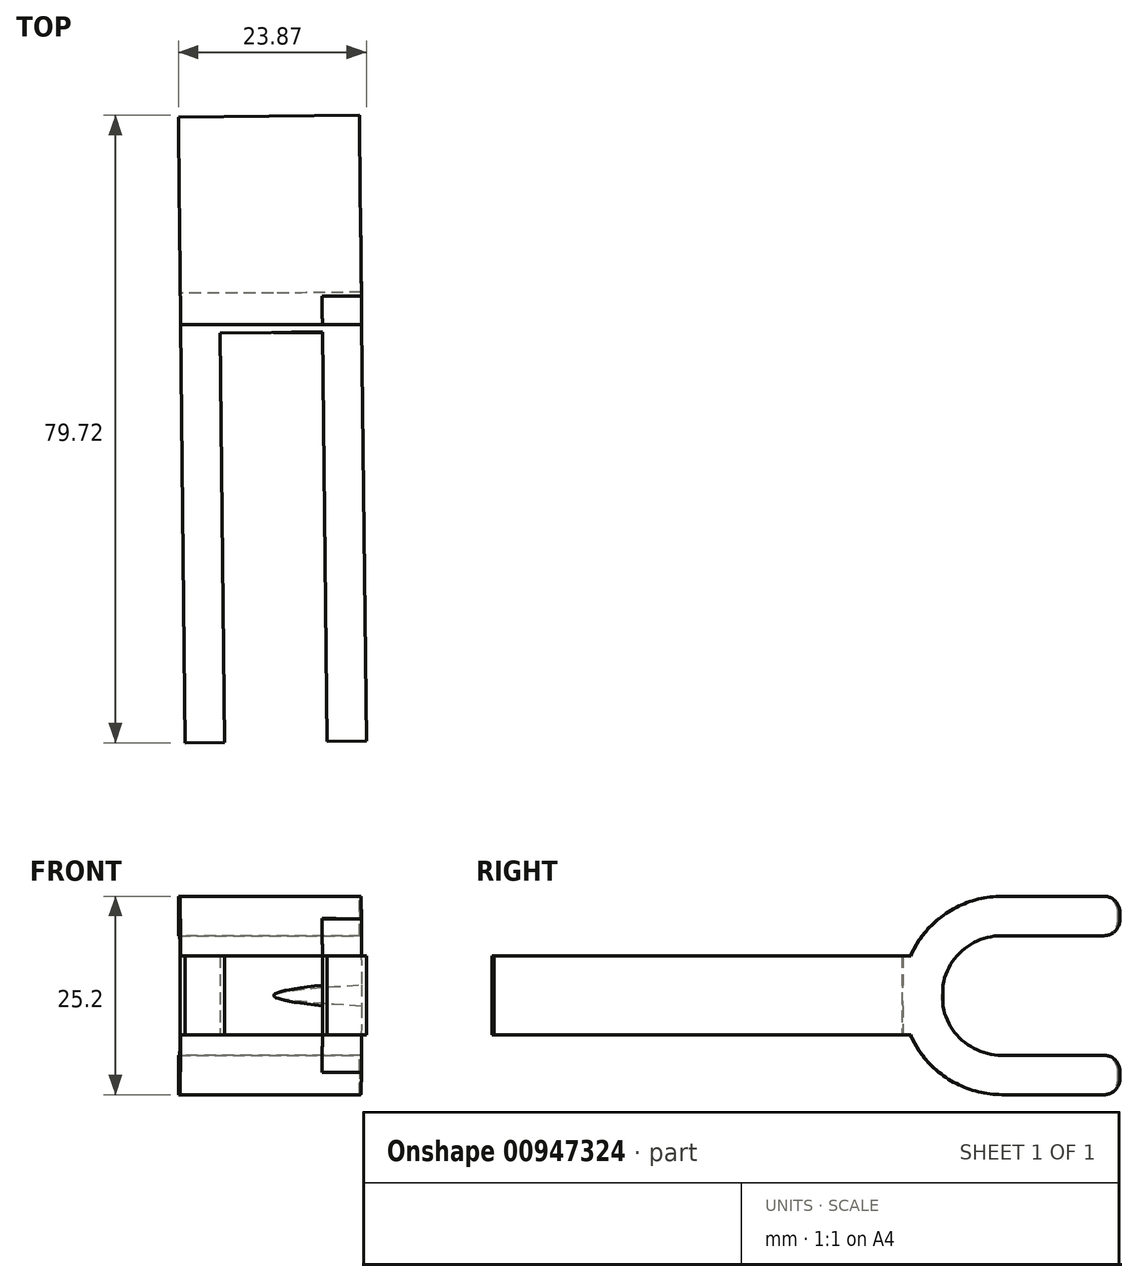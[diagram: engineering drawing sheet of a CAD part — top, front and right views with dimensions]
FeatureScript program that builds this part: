
annotation { "Feature Type Name" : "Feature", "Feature Type Description" : "" }
export const myFeature = defineFeature(function(context is Context, id is Id, definition is map)
    precondition{}
    {
        {
            var Q0;
            Q0=qCreatedBy(makeId("Top.planeOp"),FACE);
            var sketch = newSketch(context, id + "F0", { "sketchPlane" : qUnion([Q0])});
            skLineSegment(sketch, "E0.bottom", {"start": v(-6.79, 25.93) * mm, "end": v(6.21, 26.07) * mm});
            skLineSegment(sketch, "E0.left", {"start": v(-6.79, 25.93) * mm, "end": v(-6.21, -26.07) * mm});
            skLineSegment(sketch, "E0.right", {"start": v(6.21, 26.07) * mm, "end": v(6.79, -25.93) * mm});
            skPoint(sketch, "E0.middle", {"position": v(0, 0) * mm});
            skLineSegment(sketch, "E1.0", {"start": v(11.16, 31.12) * mm, "end": v(11.78, -25.87) * mm});
            skLineSegment(sketch, "E1.1", {"start": v(-11.84, 30.87) * mm, "end": v(11.16, 31.12) * mm});
            skLineSegment(sketch, "E1.2", {"start": v(-11.84, 30.87) * mm, "end": v(-11.21, -26.12) * mm});
            skLineSegment(sketch, "E2", {"start": v(-6.21, -26.07) * mm, "end": v(-11.21, -26.12) * mm});
            skLineSegment(sketch, "E3", {"start": v(6.79, -25.93) * mm, "end": v(11.78, -25.87) * mm});
            skSolve(sketch);
        }
        {
            var Q0;
            Q0=makeQuery(id+"F0.imprint","IMPRINT",FACE,{"disambiguationData":[TD([[makeQuery(id+"F0.imprint","IMPRINT",EDGE,{"derivedFrom":sQuery(id+"F0.wireOp",EDGE,"E0.bottom")}),1.0]])]});
            extrude(context, id + "F1", {"entities" : qUnion([Q0]), "depth" : 10 * mm, "offsetDistance" : 25 * mm});
        }
        {
            var Q0;
            Q0=qCreatedBy(makeId("Right.planeOp"),FACE);
            var sketch = newSketch(context, id + "F2", { "sketchPlane" : qUnion([Q0])});
            skLineSegment(sketch, "E4", {"start": v(31, 0) * mm, "end": v(31, 10) * mm});
            skLineSegment(sketch, "E5", {"start": v(31, 5) * mm, "end": v(38.6, 5) * mm, "construction": true});
            skCircle(sketch, "E6", {"center": v(38.6, 5) * mm, "radius": 7.6 * mm});
            skCircle(sketch, "E7.0", {"center": v(38.6, 5) * mm, "radius": 12.6 * mm});
            skLineSegment(sketch, "E8", {"start": v(38.6, 5) * mm, "end": v(38.6, -7.6) * mm});
            skLineSegment(sketch, "E9", {"start": v(38.6, 5) * mm, "end": v(38.6, 17.6) * mm});
            skSolve(sketch);
        }
        {
            var Q0;
            {var subQ5=sQuery(id+"F2.wireOp",EDGE,"E6");var subQ7=makeQuery(id+"F2.imprint","IMPRINT",VERTEX,{"derivedFrom":subQ5});Q0=makeQuery(id+"F2.imprint","IMPRINT",FACE,{"disambiguationData":[TD([[makeQuery(id+"F2.imprint","IMPRINT",EDGE,{"disambiguationData":[TD([[subQ7,1.0]])],"derivedFrom":subQ5}),-1.0]])]});}
            var Q1;
            Q1=makeQuery(id+"F1.opExtrude","SWEPT_FACE",FACE,{"disambiguationData":[OSD([sQuery(id+"F0.wireOp",EDGE,"E1.0")])]});
            var Q2;
            Q2=makeQuery(id+"F1.opExtrude","SWEPT_FACE",FACE,{"disambiguationData":[OSD([sQuery(id+"F0.wireOp",EDGE,"E1.2")])]});
            extrude(context, id + "F3", {"entities" : qUnion([Q0]), "operationType" : NewBodyOperationType.ADD, "endBound" : BoundingType.UP_TO_SURFACE, "depth" : 24 * mm, "endBoundEntityFace" : qUnion([Q1]), "offsetDistance" : 25 * mm, "hasSecondDirection" : true, "secondDirectionBound" : SecondDirectionBoundingType.UP_TO_SURFACE, "secondDirectionOppositeDirection" : true, "secondDirectionDepth" : 25 * mm, "secondDirectionBoundEntityFace" : qUnion([Q2])});
        }
        {
            var Q0;
            Q0=makeQuery(id+"F3.opExtrude","CAP_FACE",FACE,{"disambiguationData":[OSD([sQuery(id+"F2.wireOp",EDGE,"E6"),sQuery(id+"F2.wireOp",EDGE,"E7.0"),sQuery(id+"F2.wireOp",EDGE,"E8"),sQuery(id+"F2.wireOp",EDGE,"E9")])],"isStart":false});
            var sketch = newSketch(context, id + "F4", { "sketchPlane" : qUnion([Q0])});
            skLineSegment(sketch, "E10.bottom", {"start": v(38.48, 17.6) * mm, "end": v(53.48, 17.6) * mm});
            skLineSegment(sketch, "E10.top", {"start": v(38.48, 12.6) * mm, "end": v(53.48, 12.6) * mm});
            skLineSegment(sketch, "E10.left", {"start": v(38.48, 17.6) * mm, "end": v(38.48, 12.6) * mm});
            skLineSegment(sketch, "E10.right", {"start": v(53.48, 17.6) * mm, "end": v(53.48, 12.6) * mm});
            skLineSegment(sketch, "E11.bottom", {"start": v(38.48, -2.6) * mm, "end": v(53.48, -2.6) * mm});
            skLineSegment(sketch, "E11.top", {"start": v(38.48, -7.6) * mm, "end": v(53.48, -7.6) * mm});
            skLineSegment(sketch, "E11.left", {"start": v(38.48, -2.6) * mm, "end": v(38.48, -7.6) * mm});
            skLineSegment(sketch, "E11.right", {"start": v(53.48, -2.6) * mm, "end": v(53.48, -7.6) * mm});
            skSolve(sketch);
        }
        {
            var Q0;
            Q0=makeQuery(id+"F4.imprint","IMPRINT",FACE,{"disambiguationData":[TD([[makeQuery(id+"F4.imprint","IMPRINT",EDGE,{"derivedFrom":sQuery(id+"F4.wireOp",EDGE,"E10.bottom")}),-1.0]])]});
            var Q1;
            {var subQ0=makeQuery(id+"F1.opExtrude","SWEPT_FACE",FACE,{"disambiguationData":[OSD([sQuery(id+"F0.wireOp",EDGE,"E1.2")])]});Q1=makeQuery(id+"F3.boolean.opBoolean","MERGE",FACE,{"derivedFrom":[subQ0,makeQuery(id+"F3.opExtrude","CAP_FACE",FACE,{"disambiguationData":[OSD([sQuery(id+"F2.wireOp",EDGE,"E6"),sQuery(id+"F2.wireOp",EDGE,"E7.0"),sQuery(id+"F2.wireOp",EDGE,"E8"),sQuery(id+"F2.wireOp",EDGE,"E9")]),topologyDisambiguationEdgeConnected([subQ0])],"isStart":false})]});}
            extrude(context, id + "F5", {"entities" : qUnion([Q0]), "operationType" : NewBodyOperationType.ADD, "endBound" : BoundingType.UP_TO_SURFACE, "oppositeDirection" : true, "depth" : 25 * mm, "endBoundEntityFace" : qUnion([Q1]), "offsetDistance" : 25 * mm});
        }
        {
            var Q0;
            {var subQ0=sQuery(id+"F0.wireOp",EDGE,"E3");var subQ4=sQuery(id+"F0.wireOp",EDGE,"E1.0");Q0=makeQuery(id+"F3.boolean.opBoolean","SPLIT",FACE,{"disambiguationData":[TD([makeQuery(id+"F1.opExtrude","SWEPT_FACE",FACE,{"disambiguationData":[OSD([subQ0])]})])],"derivedFrom":makeQuery(id+"F1.opExtrude","SWEPT_FACE",FACE,{"disambiguationData":[OSD([subQ4])]})});}
            var sketch = newSketch(context, id + "F6", { "sketchPlane" : qUnion([Q0])});
            skLineSegment(sketch, "E12", {"start": v(11.5, 10) * mm, "end": v(11.5, 0) * mm, "construction": true});
            skLineSegment(sketch, "E13", {"start": v(11.5, 0) * mm, "end": v(31.5, 0) * mm});
            skLineSegment(sketch, "E14", {"start": v(1047.02, 5.94) * mm, "end": v(1047.02, 17.3) * mm});
            skLineSegment(sketch, "E15", {"start": v(31.5, 0) * mm, "end": v(31.5, -5) * mm});
            skLineSegment(sketch, "E16", {"start": v(31.5, -5) * mm, "end": v(11.5, 0) * mm});
            skLineSegment(sketch, "E17", {"start": v(11.5, 10) * mm, "end": v(31.5, 10) * mm});
            skLineSegment(sketch, "E18", {"start": v(31.5, 10) * mm, "end": v(31.5, 15) * mm});
            skLineSegment(sketch, "E19", {"start": v(31.5, 15) * mm, "end": v(11.5, 10) * mm});
            skSolve(sketch);
        }
        {
            var Q0;
            {var subQ4=sQuery(id+"F6.wireOp",EDGE,"E18");Q0=makeQuery(id+"F6.imprint","IMPRINT",FACE,{"disambiguationData":[TD([[makeQuery(id+"F6.imprint","IMPRINT",EDGE,{"derivedFrom":subQ4}),1.0]])]});}
            var Q1;
            {var subQ4=sQuery(id+"F6.wireOp",EDGE,"E15");Q1=makeQuery(id+"F6.imprint","IMPRINT",FACE,{"disambiguationData":[TD([[makeQuery(id+"F6.imprint","IMPRINT",EDGE,{"derivedFrom":subQ4}),-1.0]])]});}
            var Q2;
            Q2=makeQuery(id+"F1.opExtrude","SWEPT_FACE",FACE,{"disambiguationData":[OSD([sQuery(id+"F0.wireOp",EDGE,"E0.right")])]});
            extrude(context, id + "F7", {"entities" : qUnion([Q0, Q1]), "operationType" : NewBodyOperationType.ADD, "endBound" : BoundingType.UP_TO_SURFACE, "oppositeDirection" : true, "depth" : 25 * mm, "endBoundEntityFace" : qUnion([Q2]), "offsetDistance" : 25 * mm});
        }
        {
            var Q0;
            Q0=makeQuery(id+"F1.opExtrude","SWEPT_FACE",FACE,{"disambiguationData":[OSD([sQuery(id+"F0.wireOp",EDGE,"E1.2")])]});
            var sketch = newSketch(context, id + "F8", { "sketchPlane" : qUnion([Q0])});
            skLineSegment(sketch, "E20", {"start": v(-11.49, 0) * mm, "end": v(-11.49, 10) * mm, "construction": true});
            skLineSegment(sketch, "E21", {"start": v(-11.49, 0) * mm, "end": v(-31.49, 0) * mm});
            skLineSegment(sketch, "E22", {"start": v(-31.49, 0) * mm, "end": v(-31.49, -5) * mm});
            skLineSegment(sketch, "E23", {"start": v(-31.49, -5) * mm, "end": v(-11.49, 0) * mm});
            skLineSegment(sketch, "E24", {"start": v(-11.49, 10) * mm, "end": v(-31.49, 10) * mm});
            skLineSegment(sketch, "E25", {"start": v(-31.49, 10) * mm, "end": v(-31.49, 15) * mm});
            skLineSegment(sketch, "E26", {"start": v(-31.49, 15) * mm, "end": v(-11.49, 10) * mm});
            skSolve(sketch);
        }
        {
            var Q0;
            {var subQ4=sQuery(id+"F8.wireOp",EDGE,"E22");Q0=makeQuery(id+"F8.imprint","IMPRINT",FACE,{"disambiguationData":[TD([[makeQuery(id+"F8.imprint","IMPRINT",EDGE,{"derivedFrom":subQ4}),1.0]])]});}
            var Q1;
            {var subQ4=sQuery(id+"F8.wireOp",EDGE,"E25");Q1=makeQuery(id+"F8.imprint","IMPRINT",FACE,{"disambiguationData":[TD([[makeQuery(id+"F8.imprint","IMPRINT",EDGE,{"derivedFrom":subQ4}),-1.0]])]});}
            var Q2;
            Q2=makeQuery(id+"F1.opExtrude","SWEPT_FACE",FACE,{"disambiguationData":[OSD([sQuery(id+"F0.wireOp",EDGE,"E0.left")])]});
            extrude(context, id + "F9", {"entities" : qUnion([Q0, Q1]), "operationType" : NewBodyOperationType.ADD, "endBound" : BoundingType.UP_TO_SURFACE, "oppositeDirection" : true, "depth" : 25 * mm, "endBoundEntityFace" : qUnion([Q2]), "offsetDistance" : 25 * mm});
        }
        {
            var Q0;
            Q0=makeQuery(id+"F4.imprint","IMPRINT",FACE,{"disambiguationData":[TD([[makeQuery(id+"F4.imprint","IMPRINT",EDGE,{"derivedFrom":sQuery(id+"F4.wireOp",EDGE,"E11.bottom")}),-1.0]])]});
            var Q1;
            {var subQ0=makeQuery(id+"F1.opExtrude","SWEPT_FACE",FACE,{"disambiguationData":[OSD([sQuery(id+"F0.wireOp",EDGE,"E1.2")])]});Q1=makeQuery(id+"F5.boolean.opBoolean","MERGE",FACE,{"derivedFrom":[makeQuery(id+"F3.boolean.opBoolean","MERGE",FACE,{"derivedFrom":[subQ0,makeQuery(id+"F3.opExtrude","CAP_FACE",FACE,{"disambiguationData":[OSD([sQuery(id+"F2.wireOp",EDGE,"E6"),sQuery(id+"F2.wireOp",EDGE,"E7.0"),sQuery(id+"F2.wireOp",EDGE,"E8"),sQuery(id+"F2.wireOp",EDGE,"E9")]),topologyDisambiguationEdgeConnected([subQ0])],"isStart":false})]}),makeQuery(id+"F5.opExtrude","CAP_FACE",FACE,{"disambiguationData":[OSD([sQuery(id+"F4.wireOp",EDGE,"E10.bottom"),sQuery(id+"F4.wireOp",EDGE,"E10.top"),sQuery(id+"F4.wireOp",EDGE,"E10.left"),sQuery(id+"F4.wireOp",EDGE,"E10.right")])],"isStart":false})]});}
            extrude(context, id + "F10", {"entities" : qUnion([Q0]), "operationType" : NewBodyOperationType.ADD, "endBound" : BoundingType.UP_TO_SURFACE, "oppositeDirection" : true, "depth" : 25 * mm, "endBoundEntityFace" : qUnion([Q1]), "offsetDistance" : 25 * mm});
        }
        {
            var Q0;
            Q0=makeQuery(id+"F5.opExtrude","SWEPT_EDGE",EDGE,{"disambiguationData":[OSD([sQuery(id+"F4.wireOp",EDGE,"E10.bottom"),sQuery(id+"F4.wireOp",EDGE,"E10.right")])]});
            var Q1;
            Q1=makeQuery(id+"F5.opExtrude","SWEPT_EDGE",EDGE,{"disambiguationData":[OSD([sQuery(id+"F4.wireOp",EDGE,"E10.top"),sQuery(id+"F4.wireOp",EDGE,"E10.right")])]});
            var Q2;
            Q2=makeQuery(id+"F10.opExtrude","SWEPT_EDGE",EDGE,{"disambiguationData":[OSD([sQuery(id+"F4.wireOp",EDGE,"E11.bottom"),sQuery(id+"F4.wireOp",EDGE,"E11.right")])]});
            var Q3;
            Q3=makeQuery(id+"F10.opExtrude","SWEPT_EDGE",EDGE,{"disambiguationData":[OSD([sQuery(id+"F4.wireOp",EDGE,"E11.top"),sQuery(id+"F4.wireOp",EDGE,"E11.right")])]});
            fillet(context, id + "F11", {"entities" : qUnion([Q0, Q1, Q2, Q3]), "radius" : 2 * mm, "tangentPropagation" : true, "allowEdgeOverflow" : false});
        }
    });
